# Revit family: Lighting Fixture_Sylvania_Expospot 90 Adjustable_Ceiling Recessed1
name_source: partatom
category: Lighting Fixtures
revit_build: Autodesk Revit 2016 (Build: 20161004_0715(x64)
units: mm (PartAtom-declared; Revit-internal decimal feet)

## family parameters
Cut with Voids When Loaded = No
Host = Face
Light Source = No
OmniClass Number = 23.80.70.11.17
OmniClass Title = Specialized Lighting by Location or Use
Part Type = Normal
Room Calculation Point = No
Round Connector Dimension = Use Diameter
Shared = No

## types (24) — shared parameters
Assembly Code = D5020200
Average Life = 50 000h
Body Material = Aluminum_Sylvania_Expospot_White
Body Secondary Material = Plastic_Sylvania_Expospot_Black
Colour Variation Initial = 3SDCM
Control Gear Mounting = Remote
Control Gear Required = No
Control Gear Type = Electronic
Cutout Diameter = 140 mm
Description = Specifically designed for Retail and Display applications. I.e. Supermarkets Fashion Retail Department stores. Build around a 90mm reflector and lens combination.
Diameter = 150 mm
Dimmable = N
Drive Current = 700mA
Electrical Protection = Class II
Glow Wire Test = 850 °C
Head Diameter = 98 mm  [stored 0.321522 ft]
Head Radius = 49 mm  [stored 0.160761 ft]
Height = 103 mm  [stored 0.337927 ft]
IK Rating = IK02
IP Rating = IP20
Inrush Current = 19 A
Inrush Duration = 250µs
LOR = 100%
Lamp = LED
Light Loss Factor = 1
Manufacturer = Feilo Sylvania
Max. Luminaires per 10A B Breaker = 13
Max. Luminaires per 10A C Breaker = 21
Max. Luminaires per 13A B Breaker = 17
Max. Luminaires per 13A C Breaker = 28
Max. Luminaires per 16A B Breaker = 21
Max. Luminaires per 16A C Breaker = 35
Max. Luminaires per 20A B Breaker = 27
Max. Luminaires per 20A C Breaker = 45
Mounting Outer Radius = 52 mm
Nominal Frequency = 50/60Hz
Photobiological Risk Group = RG1
Product Family = EXPOSPOT 90 ADJUSTABLE
Product Page URL = http://www.sylvania-lighting.com
Radius = 75 mm
Reflector Material = Aluminum_Sylvania_Expospot_Polished
URL = http://www.sylvania-lighting.com
Voltage = 240 V
Voltage Comments = 220-240V~
Weight = 1 kg
zero-valued in all types: Default Elevation

## per-type parameters (varying)
| type | Apparent Load | Beam Angle | CRI | Diffuser Material | Initial Color | Initial Intensity | Lamp Power Factor | Photometric Web File | Product Code | Total Power Consumption |
| EXPOSPOT 90 ADJ HO 90 4K WB WH | 35 VA | 57° | 90Ra | Acrylic_Sylvania_Expospot_4000K | 4000 K | 3479 lm | 0.95 | IES_Expospot_90_Adjustable : 0060296 | 0060296 | 35 W |
| EXPOSPOT 90 ADJ HO 90 4K MB WH | 35 VA | 43° | 90Ra | Acrylic_Sylvania_Expospot_4000K | 4000 K | 3458 lm | 0.95 | IES_Expospot_90_Adjustable : 0060295 | 0060295 | 35 W |
| EXPOSPOT 90 ADJ HO 90 4K NB WH | 35 VA | 26° | 90Ra | Acrylic_Sylvania_Expospot_4000K | 4000 K | 3570 lm | 0.95 | IES_Expospot_90_Adjustable : 0060294 | 0060294 | 35 W |
| EXPOSPOT 90 ADJ HO 90 3K WB WH | 35 VA | 56° | 90Ra | Acrylic_Sylvania_Expospot_3000K | 3000 K | 3293 lm | 0.95 | IES_Expospot_90_Adjustable : 0060293 | 0060293 | 35 W |
| EXPOSPOT 90 ADJ HO 90 3K MB WH | 35 VA | 44° | 90Ra | Acrylic_Sylvania_Expospot_3000K | 3000 K | 3180 lm | 0.95 | IES_Expospot_90_Adjustable : 0060292 | 0060292 | 35 W |
| EXPOSPOT 90 ADJ HO 90 3K NB WH | 35 VA | 26° | 90Ra | Acrylic_Sylvania_Expospot_3000K | 3000 K | 3369 lm | 0.95 | IES_Expospot_90_Adjustable : 0060291 | 0060291 | 35 W |
| EXPOSPOT 90 ADJ HO 80 4K WB WH | 35 VA | 60° | 80Ra | Acrylic_Sylvania_Expospot_4000K | 4000 K | 3942 lm | 0.95 | IES_Expospot_90_Adjustable : 0060290 | 0060290 | 35 W |
| EXPOSPOT 90 ADJ HO 80 4K MB WH | 35 VA | 43° | 80Ra | Acrylic_Sylvania_Expospot_4000K | 4000 K | 3852 lm | 0.95 | IES_Expospot_90_Adjustable : 0060289 | 0060289 | 35 W |
| EXPOSPOT 90 ADJ HO 80 4K NB WH | 35 VA | 27° | 80Ra | Acrylic_Sylvania_Expospot_4000K | 4000 K | 4121 lm | 0.95 | IES_Expospot_90_Adjustable : 0060288 | 0060288 | 35 W |
| EXPOSPOT 90 ADJ HO 80 3K WB WH | 35 VA | 62° | 80Ra | Acrylic_Sylvania_Expospot_3000K | 3000 K | 3736 lm | 0.95 | IES_Expospot_90_Adjustable : 0060287 | 0060287 | 35 W |
| EXPOSPOT 90 ADJ HO 80 3K MB WH | 35 VA | 45° | 80Ra | Acrylic_Sylvania_Expospot_3000K | 3000 K | 3721 lm | 0.95 | IES_Expospot_90_Adjustable : 0060286 | 0060286 | 35 W |
| EXPOSPOT 90 ADJ HE 90 4K WB WH | 28 VA | 57° | 90Ra | Acrylic_Sylvania_Expospot_4000K | 4000 K | 2855 lm | 0.92 | IES_Expospot_90_Adjustable : 0060272 | 0060272 | 28 W |
| EXPOSPOT 90 ADJ HE 90 4K MB WH | 28 VA | 45° | 90Ra | Acrylic_Sylvania_Expospot_4000K | 4000 K | 2836 lm | 0.92 | IES_Expospot_90_Adjustable : 0060271 | 0060271 | 28 W |
| EXPOSPOT 90 ADJ HE 90 4K NB WH | 28 VA | 26° | 90Ra | Acrylic_Sylvania_Expospot_4000K | 4000 K | 2789 lm | 0.92 | IES_Expospot_90_Adjustable : 0060270 | 0060270 | 28 W |
| EXPOSPOT 90 ADJ HE 90 3K WB WH | 28 VA | 58° | 90Ra | Acrylic_Sylvania_Expospot_3000K | 3000 K | 2589 lm | 0.92 | IES_Expospot_90_Adjustable : 0060269 | 0060269 | 28 W |
| EXPOSPOT 90 ADJ HE 90 3K MB WH | 28 VA | 44° | 90Ra | Acrylic_Sylvania_Expospot_3000K | 3000 K | 2573 lm | 0.92 | IES_Expospot_90_Adjustable : 0060268 | 0060268 | 28 W |
| EXPOSPOT 90 ADJ HE 90 3K NB WH | 28 VA | 25° | 90Ra | Acrylic_Sylvania_Expospot_3000K | 3000 K | 2536 lm | 0.92 | IES_Expospot_90_Adjustable : 0060267 | 0060267 | 28 W |
| EXPOSPOT 90 ADJ HE 80 4K WB WH | 28 VA | 57° | 80Ra | Acrylic_Sylvania_Expospot_4000K | 4000 K | 3229 lm | 0.92 | IES_Expospot_90_Adjustable : 0060266 | 0060266 | 28 W |
| EXPOSPOT 90 ADJ HE 80 4K MB WH | 28 VA | 43° | 80Ra | Acrylic_Sylvania_Expospot_4000K | 4000 K | 3232 lm | 0.92 | IES_Expospot_90_Adjustable : 0060265 | 0060265 | 28 W |
| EXPOSPOT 90 ADJ HE 80 4K NB WH | 28 VA | 29° | 80Ra | Acrylic_Sylvania_Expospot_4000K | 4000 K | 3145 lm | 0.92 | IES_Expospot_90_Adjustable : 0060264 | 0060264 | 28 W |
| EXPOSPOT 90 ADJ HE 80 3K WB WH | 28 VA | 61° | 80Ra | Acrylic_Sylvania_Expospot_3000K | 3000 K | 3174 lm | 0.92 | IES_Expospot_90_Adjustable : 0060263 | 0060263 | 28 W |
| EXPOSPOT 90 ADJ HE 80 3K MB WH | 28 VA | 47° | 80Ra | Acrylic_Sylvania_Expospot_3000K | 3000 K | 3126 lm | 0.92 | IES_Expospot_90_Adjustable : 0060262 | 0060262 | 28 W |
| EXPOSPOT 90 ADJ HE 80 3K NB WH | 28 VA | 26° | 80Ra | Acrylic_Sylvania_Expospot_3000K | 3000 K | 3174 lm | 0.92 | IES_Expospot_90_Adjustable : 0060261 | 0060261 | 28 W |
| EXPOSPOT 90 ADJ HO 80 3K NB WH | 35 VA | 27° | 80Ra | Acrylic_Sylvania_Expospot_3000K | 3000 K | 3946 lm | 0.95 | IES_Expospot_90_Adjustable : 0060285 | 0060285 | 35 W |

note: column(s) folded — value = type name in every type: Model

note: [stored X ft] marks values corroborated as IEEE doubles in the binary element streams (Revit-internal decimal feet)

## geometry (parser evidence)
native form markers: Sweep x7
no freeform markers — native parametric forms only
